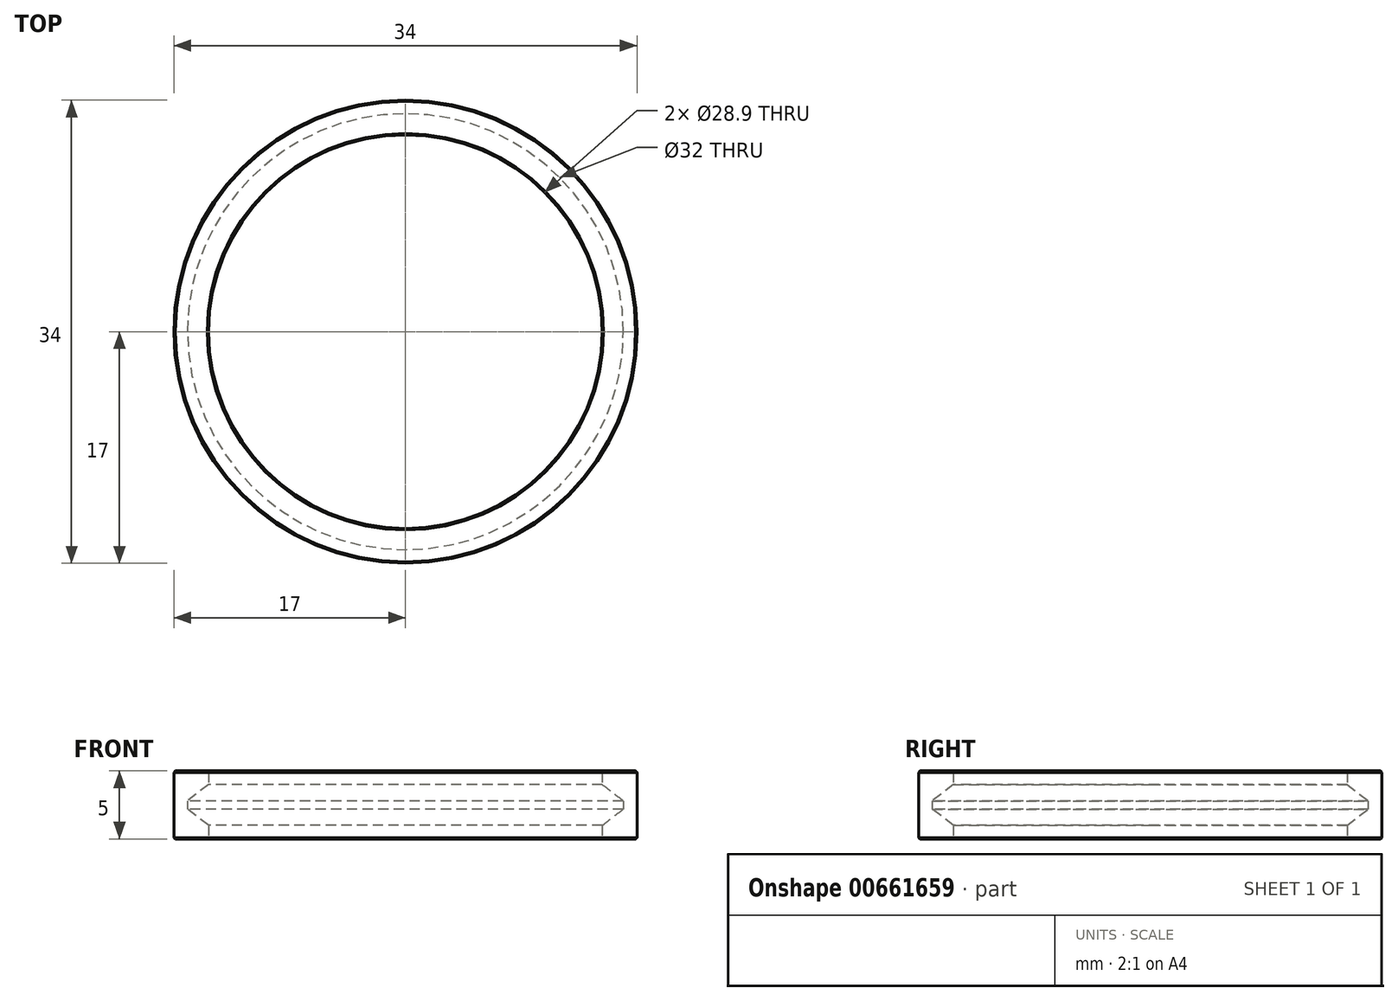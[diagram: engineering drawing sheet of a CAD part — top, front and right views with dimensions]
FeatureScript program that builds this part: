
annotation { "Feature Type Name" : "Feature", "Feature Type Description" : "" }
export const myFeature = defineFeature(function(context is Context, id is Id, definition is map)
    precondition{}
    {
        {
            var Q0;
            Q0=qCreatedBy(makeId("Top.planeOp"),FACE);
            var sketch = newSketch(context, id + "F0", { "sketchPlane" : qUnion([Q0])});
            skCircle(sketch, "E0", {"center": v(0, 0) * mm, "radius": 14.45 * mm});
            skCircle(sketch, "E1", {"center": v(0, 0) * mm, "radius": 17 * mm});
            skCircle(sketch, "E2", {"center": v(0, 0) * mm, "radius": 16 * mm});
            skSolve(sketch);
        }
        {
            var Q0;
            Q0=makeQuery(id+"F0.imprint","IMPRINT",FACE,{"disambiguationData":[TD([[makeQuery(id+"F0.imprint","IMPRINT",EDGE,{"derivedFrom":sQuery(id+"F0.wireOp",EDGE,"E0")}),-1.0]])]});
            var Q1;
            Q1=makeQuery(id+"F0.imprint","IMPRINT",FACE,{"disambiguationData":[TD([[makeQuery(id+"F0.imprint","IMPRINT",EDGE,{"derivedFrom":sQuery(id+"F0.wireOp",EDGE,"E1")}),1.0]])]});
            extrude(context, id + "F1", {"entities" : qUnion([Q0, Q1]), "endBound" : BoundingType.SYMMETRIC, "depth" : 5 * mm, "offsetDistance" : 25 * mm});
        }
        {
            var Q0;
            Q0=makeQuery(id+"F0.imprint","IMPRINT",FACE,{"disambiguationData":[TD([[makeQuery(id+"F0.imprint","IMPRINT",EDGE,{"derivedFrom":sQuery(id+"F0.wireOp",EDGE,"E0")}),-1.0]])]});
            var Q1;
            Q1=makeQuery(id+"F1.opExtrude","CAP_FACE",FACE,{"disambiguationData":[OSD([sQuery(id+"F0.wireOp",EDGE,"E0"),sQuery(id+"F0.wireOp",EDGE,"E1")])],"isStart":false});
            var Q2;
            Q2=makeQuery(id+"F1.opExtrude","CAP_FACE",FACE,{"disambiguationData":[OSD([sQuery(id+"F0.wireOp",EDGE,"E0"),sQuery(id+"F0.wireOp",EDGE,"E1")])],"isStart":true});
            extrude(context, id + "F2", {"entities" : qUnion([Q0]), "operationType" : NewBodyOperationType.REMOVE, "endBound" : BoundingType.UP_TO_SURFACE, "depth" : 25 * mm, "endBoundEntityFace" : qUnion([Q1]), "hasOffset" : true, "offsetDistance" : 1 * mm, "hasSecondDirection" : true, "secondDirectionBound" : SecondDirectionBoundingType.UP_TO_SURFACE, "secondDirectionOppositeDirection" : true, "secondDirectionDepth" : 25 * mm, "secondDirectionBoundEntityFace" : qUnion([Q2]), "hasSecondDirectionOffset" : true, "secondDirectionOffsetDistance" : 1 * mm});
        }
        {
            var Q0;
            Q0=makeQuery(id+"F2.boolean.opBoolean","COPY",EDGE,{"derivedFrom":makeQuery(id+"F2.opExtrude","CAP_EDGE",EDGE,{"disambiguationData":[OSD([sQuery(id+"F0.wireOp",EDGE,"E2")])],"isStart":true})});
            var Q1;
            Q1=makeQuery(id+"F2.boolean.opBoolean","COPY",EDGE,{"derivedFrom":makeQuery(id+"F2.opExtrude","CAP_EDGE",EDGE,{"disambiguationData":[OSD([sQuery(id+"F0.wireOp",EDGE,"E2")])],"isStart":false})});
            chamfer(context, id + "F3", {"entities" : qUnion([Q0, Q1]), "chamferType" : ChamferType.TWO_OFFSETS, "width1" : 1.55 * mm, "oppositeDirection" : false, "width2" : 1.2 * mm, "tangentPropagation" : true});
        }
        {
            var Q0;
            Q0=makeQuery(id+"F1.opExtrude","CAP_EDGE",EDGE,{"disambiguationData":[OSD([sQuery(id+"F0.wireOp",EDGE,"E1")])],"isStart":false});
            var Q1;
            Q1=makeQuery(id+"F1.opExtrude","CAP_EDGE",EDGE,{"disambiguationData":[OSD([sQuery(id+"F0.wireOp",EDGE,"E1")])],"isStart":true});
            chamfer(context, id + "F4", {"entities" : qUnion([Q0, Q1]), "width" : 0.1 * mm, "tangentPropagation" : true});
        }
        {
            var Q0;
            Q0=makeQuery(id+"F1.opExtrude","CAP_FACE",FACE,{"disambiguationData":[OSD([sQuery(id+"F0.wireOp",EDGE,"E0"),sQuery(id+"F0.wireOp",EDGE,"E1")])],"isStart":false});
            var sketch = newSketch(context, id + "F5", { "sketchPlane" : qUnion([Q0])});
            skPoint(sketch, "E3.0", {"position": v(0, 0) * mm});
            skCircle(sketch, "E4.0", {"center": v(0, 0) * mm, "radius": 14.45 * mm});
            skCircle(sketch, "E5.0", {"center": v(0, 0) * mm, "radius": 17 * mm});
            skCircle(sketch, "E6", {"center": v(0, 0) * mm, "radius": 14.97 * mm, "construction": true});
            skCircle(sketch, "E7.0", {"center": v(0, 0) * mm, "radius": 16.9 * mm});
            skCircle(sketch, "E8.cCircle", {"center": v(0, 0) * mm, "radius": 14.95 * mm, "construction": true});
            skLineSegment(sketch, "E8.0", {"start": v(-3.72, -14.5) * mm, "end": v(-5.51, -13.92) * mm});
            skLineSegment(sketch, "E8.1", {"start": v(-5.51, -13.92) * mm, "end": v(-7.21, -13.12) * mm});
            skLineSegment(sketch, "E8.2", {"start": v(-7.21, -13.12) * mm, "end": v(-8.8, -12.12) * mm});
            skLineSegment(sketch, "E8.3", {"start": v(-8.8, -12.12) * mm, "end": v(-10.25, -10.92) * mm});
            skLineSegment(sketch, "E8.4", {"start": v(-10.25, -10.92) * mm, "end": v(-11.54, -9.55) * mm});
            skLineSegment(sketch, "E8.5", {"start": v(-11.54, -9.55) * mm, "end": v(-12.64, -8.02) * mm});
            skLineSegment(sketch, "E8.6", {"start": v(-12.64, -8.02) * mm, "end": v(-13.55, -6.38) * mm});
            skLineSegment(sketch, "E8.7", {"start": v(-13.55, -6.38) * mm, "end": v(-14.24, -4.63) * mm});
            skLineSegment(sketch, "E8.8", {"start": v(-14.24, -4.63) * mm, "end": v(-14.7, -2.8) * mm});
            skLineSegment(sketch, "E8.9", {"start": v(-14.7, -2.8) * mm, "end": v(-14.95, -0.94) * mm});
            skLineSegment(sketch, "E8.10", {"start": v(-14.95, -0.94) * mm, "end": v(-14.95, 0.94) * mm});
            skLineSegment(sketch, "E8.11", {"start": v(-14.95, 0.94) * mm, "end": v(-14.7, 2.8) * mm});
            skLineSegment(sketch, "E8.12", {"start": v(-14.7, 2.8) * mm, "end": v(-14.24, 4.63) * mm});
            skLineSegment(sketch, "E8.13", {"start": v(-14.24, 4.63) * mm, "end": v(-13.55, 6.38) * mm});
            skLineSegment(sketch, "E8.14", {"start": v(-13.55, 6.38) * mm, "end": v(-12.64, 8.02) * mm});
            skLineSegment(sketch, "E8.15", {"start": v(-12.64, 8.02) * mm, "end": v(-11.54, 9.55) * mm});
            skLineSegment(sketch, "E8.16", {"start": v(-11.54, 9.55) * mm, "end": v(-10.25, 10.92) * mm});
            skLineSegment(sketch, "E8.17", {"start": v(-10.25, 10.92) * mm, "end": v(-8.8, 12.12) * mm});
            skLineSegment(sketch, "E8.18", {"start": v(-8.8, 12.12) * mm, "end": v(-7.21, 13.12) * mm});
            skLineSegment(sketch, "E8.19", {"start": v(-7.21, 13.12) * mm, "end": v(-5.51, 13.92) * mm});
            skLineSegment(sketch, "E8.20", {"start": v(-5.51, 13.92) * mm, "end": v(-3.72, 14.5) * mm});
            skLineSegment(sketch, "E8.21", {"start": v(-3.72, 14.5) * mm, "end": v(-1.88, 14.86) * mm});
            skLineSegment(sketch, "E8.22", {"start": v(-1.88, 14.86) * mm, "end": v(0, 14.97) * mm});
            skLineSegment(sketch, "E8.23", {"start": v(0, 14.97) * mm, "end": v(1.88, 14.86) * mm});
            skLineSegment(sketch, "E8.24", {"start": v(1.88, 14.86) * mm, "end": v(3.72, 14.5) * mm});
            skLineSegment(sketch, "E8.25", {"start": v(3.72, 14.5) * mm, "end": v(5.51, 13.92) * mm});
            skLineSegment(sketch, "E8.26", {"start": v(5.51, 13.92) * mm, "end": v(7.21, 13.12) * mm});
            skLineSegment(sketch, "E8.27", {"start": v(7.21, 13.12) * mm, "end": v(8.8, 12.12) * mm});
            skLineSegment(sketch, "E8.28", {"start": v(8.8, 12.12) * mm, "end": v(10.25, 10.92) * mm});
            skLineSegment(sketch, "E8.29", {"start": v(10.25, 10.92) * mm, "end": v(11.54, 9.55) * mm});
            skLineSegment(sketch, "E8.30", {"start": v(11.54, 9.55) * mm, "end": v(12.64, 8.02) * mm});
            skLineSegment(sketch, "E8.31", {"start": v(12.64, 8.02) * mm, "end": v(13.55, 6.38) * mm});
            skLineSegment(sketch, "E8.32", {"start": v(13.55, 6.38) * mm, "end": v(14.24, 4.63) * mm});
            skLineSegment(sketch, "E8.33", {"start": v(14.24, 4.63) * mm, "end": v(14.7, 2.8) * mm});
            skLineSegment(sketch, "E8.34", {"start": v(14.7, 2.8) * mm, "end": v(14.95, 0.94) * mm});
            skLineSegment(sketch, "E8.35", {"start": v(14.95, 0.94) * mm, "end": v(14.95, -0.94) * mm});
            skLineSegment(sketch, "E8.36", {"start": v(14.95, -0.94) * mm, "end": v(14.7, -2.8) * mm});
            skLineSegment(sketch, "E8.37", {"start": v(14.7, -2.8) * mm, "end": v(14.24, -4.63) * mm});
            skLineSegment(sketch, "E8.38", {"start": v(14.24, -4.63) * mm, "end": v(13.55, -6.38) * mm});
            skLineSegment(sketch, "E8.39", {"start": v(13.55, -6.38) * mm, "end": v(12.64, -8.02) * mm});
            skLineSegment(sketch, "E8.40", {"start": v(12.64, -8.02) * mm, "end": v(11.54, -9.55) * mm});
            skLineSegment(sketch, "E8.41", {"start": v(11.54, -9.55) * mm, "end": v(10.25, -10.92) * mm});
            skLineSegment(sketch, "E8.42", {"start": v(10.25, -10.92) * mm, "end": v(8.8, -12.12) * mm});
            skLineSegment(sketch, "E8.43", {"start": v(8.8, -12.12) * mm, "end": v(7.21, -13.12) * mm});
            skLineSegment(sketch, "E8.44", {"start": v(7.21, -13.12) * mm, "end": v(5.51, -13.92) * mm});
            skLineSegment(sketch, "E8.45", {"start": v(5.51, -13.92) * mm, "end": v(3.72, -14.5) * mm});
            skLineSegment(sketch, "E8.46", {"start": v(3.72, -14.5) * mm, "end": v(1.88, -14.86) * mm});
            skLineSegment(sketch, "E8.47", {"start": v(1.88, -14.86) * mm, "end": v(0, -14.97) * mm});
            skLineSegment(sketch, "E8.48", {"start": v(0, -14.97) * mm, "end": v(-1.88, -14.86) * mm});
            skLineSegment(sketch, "E8.49", {"start": v(-1.88, -14.86) * mm, "end": v(-3.72, -14.5) * mm});
            skPoint(sketch, "E8.0.midPoint", {"position": v(-4.62, -14.21) * mm});
            skLineSegment(sketch, "E9", {"start": v(0, 0) * mm, "end": v(0, 14.97) * mm, "construction": true});
            skLineSegment(sketch, "E10", {"start": v(0, 0) * mm, "end": v(1.88, 14.86) * mm, "construction": true});
            skLineSegment(sketch, "E11", {"start": v(0, 0) * mm, "end": v(3.72, 14.5) * mm, "construction": true});
            skText(sketch, "E12", { "text": "7", "fontName": "OpenSans-Regular.ttf"});
            skText(sketch, "E13", { "text": "8", "fontName": "OpenSans-Regular.ttf"});
            skText(sketch, "E14", { "text": "6", "fontName": "OpenSans-Regular.ttf"});
            skLineSegment(sketch, "E15", {"start": v(0, 0) * mm, "end": v(7.21, 13.12) * mm, "construction": true});
            skText(sketch, "E16", { "text": "C", "fontName": "OpenSans-Regular.ttf"});
            const initialGuessF5  = {"E12": [-0.00061, 0.01497, 1, 0, 0.0015], "E13": [0.00313, 0.01466, 0.96858, -0.24869, 0.0015], "E14": [0.00127, 0.01493, 0.99211, -0.12533, 0.0015], "E16": [0.0066, 0.01346, 0.8763, -0.48175, 0.0015]};
            skSetInitialGuess(sketch, initialGuessF5);
            skSolve(sketch);
        }
        {
            var Q0;
            Q0=makeQuery(id+"F1.opExtrude","CAP_EDGE",EDGE,{"disambiguationData":[OSD([sQuery(id+"F0.wireOp",EDGE,"E0")])],"isStart":false});
            var Q1;
            Q1=makeQuery(id+"F1.opExtrude","CAP_EDGE",EDGE,{"disambiguationData":[OSD([sQuery(id+"F0.wireOp",EDGE,"E0")])],"isStart":true});
            chamfer(context, id + "F6", {"entities" : qUnion([Q0, Q1]), "width" : 0.1 * mm, "tangentPropagation" : true});
        }
    });
